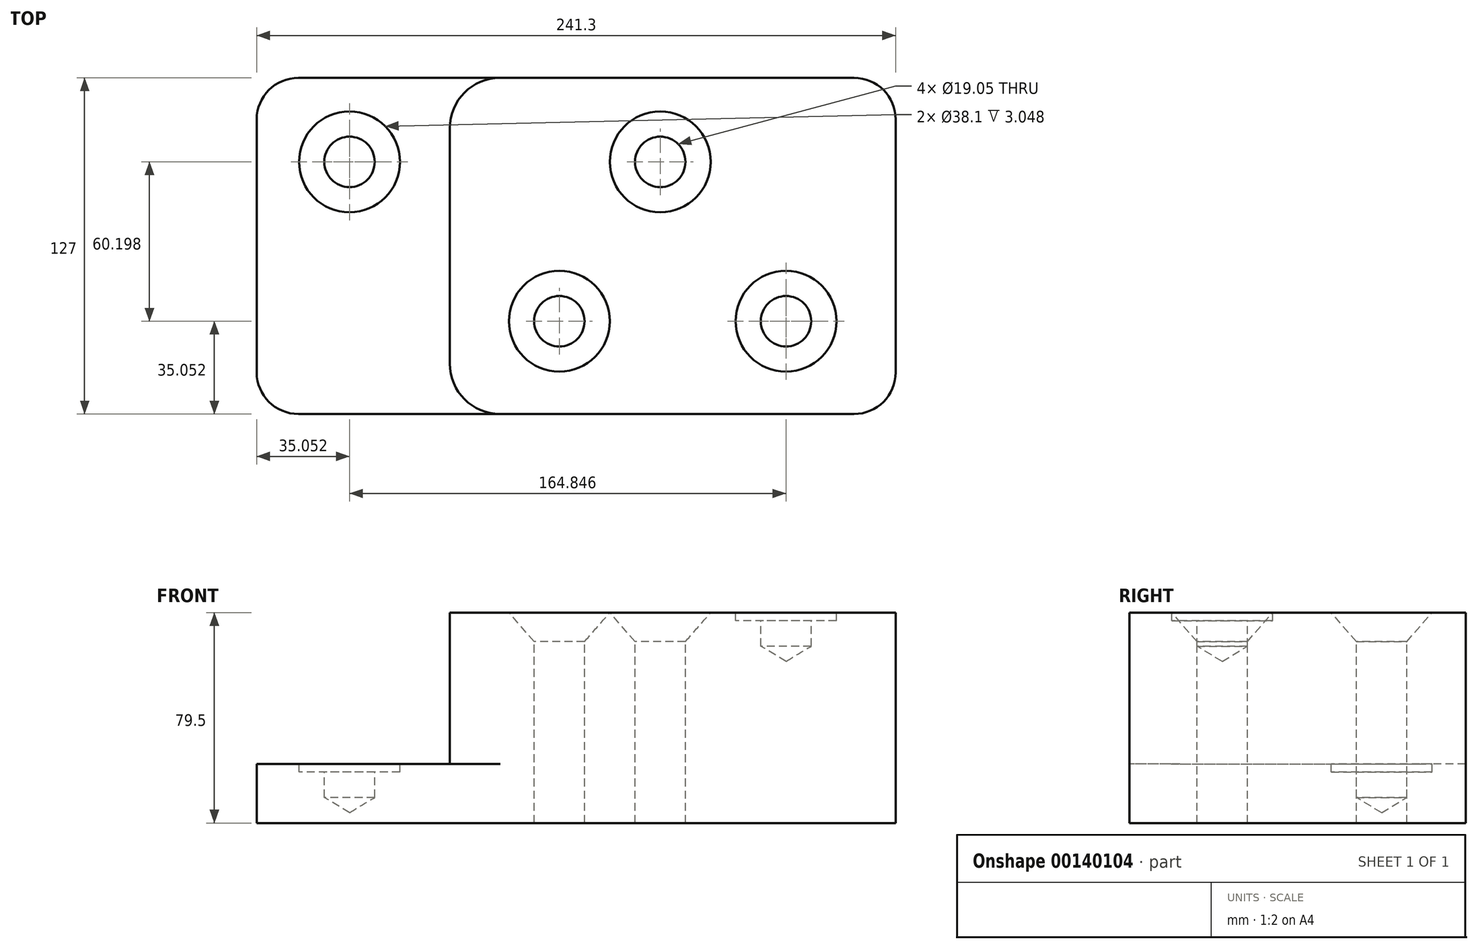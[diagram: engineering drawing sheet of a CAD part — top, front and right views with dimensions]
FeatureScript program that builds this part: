
annotation { "Feature Type Name" : "Feature", "Feature Type Description" : "" }
export const myFeature = defineFeature(function(context is Context, id is Id, definition is map)
    precondition{}
    {
        {
            var Q0;
            Q0=qCreatedBy(makeId("Top.planeOp"),FACE);
            var sketch = newSketch(context, id + "F0", { "sketchPlane" : qUnion([Q0])});
            skLineSegment(sketch, "E0.bottom", {"start": v(0, 0) * mm, "end": v(72.9, 0) * mm});
            skLineSegment(sketch, "E0.top", {"start": v(0, 127) * mm, "end": v(72.9, 127) * mm});
            skLineSegment(sketch, "E0.left", {"start": v(0, 0) * mm, "end": v(0, 127) * mm});
            skLineSegment(sketch, "E0.right", {"start": v(72.9, 0) * mm, "end": v(72.9, 127) * mm});
            skLineSegment(sketch, "E1.bottom", {"start": v(72.9, 0) * mm, "end": v(241.3, 0) * mm});
            skLineSegment(sketch, "E1.top", {"start": v(72.9, 127) * mm, "end": v(241.3, 127) * mm});
            skLineSegment(sketch, "E1.right", {"start": v(241.3, 0) * mm, "end": v(241.3, 127) * mm});
            skArc(sketch, "E2", {"start": v(91.95, 127) * mm, "mid": v(78.48, 121.42) * mm, "end": v(72.9, 107.95) * mm});
            skArc(sketch, "E3", {"start": v(72.9, 19.05) * mm, "mid": v(78.48, 5.58) * mm, "end": v(91.95, 0) * mm});
            skSolve(sketch);
        }
        {
            var Q0;
            {var subQ3=sQuery(id+"F0.wireOp",EDGE,"E2");Q0=makeQuery(id+"F0.imprint","IMPRINT",FACE,{"disambiguationData":[TD([[makeQuery(id+"F0.imprint","IMPRINT",EDGE,{"derivedFrom":subQ3}),-1.0]])]});}
            var Q1;
            {var subQ3=sQuery(id+"F0.wireOp",EDGE,"E3");Q1=makeQuery(id+"F0.imprint","IMPRINT",FACE,{"disambiguationData":[TD([[makeQuery(id+"F0.imprint","IMPRINT",EDGE,{"derivedFrom":subQ3}),-1.0]])]});}
            var Q2;
            {var subQ1=sQuery(id+"F0.wireOp",EDGE,"E0.bottom");Q2=makeQuery(id+"F0.imprint","IMPRINT",FACE,{"disambiguationData":[TD([[makeQuery(id+"F0.imprint","IMPRINT",EDGE,{"derivedFrom":subQ1}),1.0]])]});}
            extrude(context, id + "F1", {"entities" : qUnion([Q0, Q1, Q2]), "depth" : 22.35 * mm});
        }
        {
            var Q0;
            {var subQ0=sQuery(id+"F0.wireOp",EDGE,"E1.right");Q0=makeQuery(id+"F0.imprint","IMPRINT",FACE,{"disambiguationData":[TD([[makeQuery(id+"F0.imprint","IMPRINT",EDGE,{"derivedFrom":subQ0}),1.0]])]});}
            var sketch = newSketch(context, id + "F2", { "sketchPlane" : qUnion([Q0])});
            skArc(sketch, "E4.0.0", {"start": v(72.9, 19.05) * mm, "mid": v(78.48, 5.58) * mm, "end": v(91.95, 0) * mm});
            skLineSegment(sketch, "E4.0.1", {"start": v(91.95, 0) * mm, "end": v(241.3, 0) * mm});
            skLineSegment(sketch, "E4.0.2", {"start": v(241.3, 0) * mm, "end": v(241.3, 127) * mm});
            skLineSegment(sketch, "E4.0.3", {"start": v(241.3, 127) * mm, "end": v(91.95, 127) * mm});
            skArc(sketch, "E4.0.4", {"start": v(91.95, 127) * mm, "mid": v(78.48, 121.42) * mm, "end": v(72.9, 107.95) * mm});
            skLineSegment(sketch, "E4.0.5", {"start": v(72.9, 107.95) * mm, "end": v(72.9, 19.05) * mm});
            skSolve(sketch);
        }
        {
            var Q0;
            Q0 = qSketchRegion(id + "F2", true);
            extrude(context, id + "F3", {"entities" : qUnion([Q0]), "operationType" : NewBodyOperationType.ADD, "depth" : 79.5 * mm});
        }
        {
            var Q0;
            Q0=makeQuery(id+"F1.opExtrude","CAP_FACE",FACE,{"disambiguationData":[OSD([sQuery(id+"F0.wireOp",EDGE,"E0.bottom"),sQuery(id+"F0.wireOp",EDGE,"E0.top"),sQuery(id+"F0.wireOp",EDGE,"E0.left"),sQuery(id+"F0.wireOp",EDGE,"E1.bottom"),sQuery(id+"F0.wireOp",EDGE,"E1.top"),sQuery(id+"F0.wireOp",EDGE,"E0.right"),sQuery(id+"F0.wireOp",EDGE,"E2"),sQuery(id+"F0.wireOp",EDGE,"E3")])],"isStart":false});
            var sketch = newSketch(context, id + "F4", { "sketchPlane" : qUnion([Q0])});
            skCircle(sketch, "E5", {"center": v(35.05, 95.25) * mm, "radius": 9.53 * mm});
            skCircle(sketch, "E6", {"center": v(152.4, 95.25) * mm, "radius": 9.53 * mm});
            skCircle(sketch, "E7", {"center": v(114.3, 35.05) * mm, "radius": 9.53 * mm});
            skCircle(sketch, "E8", {"center": v(199.9, 35.05) * mm, "radius": 9.53 * mm});
            skSolve(sketch);
        }
        {
            var Q0;
            Q0=makeQuery(id+"F3.opExtrude","CAP_FACE",FACE,{"disambiguationData":[OSD([sQuery(id+"F2.wireOp",EDGE,"E4.0.0"),sQuery(id+"F2.wireOp",EDGE,"E4.0.1"),sQuery(id+"F2.wireOp",EDGE,"E4.0.2"),sQuery(id+"F2.wireOp",EDGE,"E4.0.3"),sQuery(id+"F2.wireOp",EDGE,"E4.0.4"),sQuery(id+"F2.wireOp",EDGE,"E4.0.5")])],"isStart":false});
            var sketch = newSketch(context, id + "F5", { "sketchPlane" : qUnion([Q0])});
            skPoint(sketch, "E9", {"position": v(152.4, 95.25) * mm});
            skPoint(sketch, "E10", {"position": v(199.9, 35.05) * mm});
            skPoint(sketch, "E11", {"position": v(114.3, 35.05) * mm});
            skPoint(sketch, "E12", {"position": v(35.05, 95.25) * mm});
            skSolve(sketch);
        }
        {
            var Q0;
            Q0=sQuery(id+"F5.wireOp",VERTEX,"E10");
            var Q1;
            Q1=sQuery(id+"F5.wireOp",VERTEX,"E12");
            var Q2;
            Q2=makeQuery(id+"F1.opExtrude","SWEPT_BODY",BODY,{"disambiguationData":[OSD([sQuery(id+"F0.wireOp",EDGE,"E0.bottom"),sQuery(id+"F0.wireOp",EDGE,"E0.top"),sQuery(id+"F0.wireOp",EDGE,"E0.left"),sQuery(id+"F0.wireOp",EDGE,"E1.bottom"),sQuery(id+"F0.wireOp",EDGE,"E1.top"),sQuery(id+"F0.wireOp",EDGE,"E0.right"),sQuery(id+"F0.wireOp",EDGE,"E2"),sQuery(id+"F0.wireOp",EDGE,"E3")])]});
            hole(context, id + "F6", {"style" : HoleStyle.C_BORE, "endStyle" : HoleEndStyle.BLIND, "holeDiameter" : 19.05 * mm, "cBoreDiameter" : 38.1 * mm, "cBoreDepth" : 3.05 * mm, "holeDepth" : 12.7 * mm, "locations" : qUnion([Q0, Q1]), "scope" : qUnion([Q2])});
        }
        {
            var Q0;
            Q0=makeQuery(id+"F3.opExtrude","CAP_FACE",FACE,{"disambiguationData":[OSD([sQuery(id+"F2.wireOp",EDGE,"E4.0.0"),sQuery(id+"F2.wireOp",EDGE,"E4.0.1"),sQuery(id+"F2.wireOp",EDGE,"E4.0.2"),sQuery(id+"F2.wireOp",EDGE,"E4.0.3"),sQuery(id+"F2.wireOp",EDGE,"E4.0.4"),sQuery(id+"F2.wireOp",EDGE,"E4.0.5")])],"isStart":false});
            var sketch = newSketch(context, id + "F7", { "sketchPlane" : qUnion([Q0])});
            skPoint(sketch, "E13", {"position": v(152.4, 95.25) * mm});
            skPoint(sketch, "E14", {"position": v(114.3, 35.05) * mm});
            skSolve(sketch);
        }
        {
            var Q0;
            Q0=sQuery(id+"F7.wireOp",VERTEX,"E13");
            var Q1;
            Q1=sQuery(id+"F7.wireOp",VERTEX,"E14");
            var Q2;
            Q2=makeQuery(id+"F1.opExtrude","SWEPT_BODY",BODY,{"disambiguationData":[OSD([sQuery(id+"F0.wireOp",EDGE,"E0.bottom"),sQuery(id+"F0.wireOp",EDGE,"E0.top"),sQuery(id+"F0.wireOp",EDGE,"E0.left"),sQuery(id+"F0.wireOp",EDGE,"E1.bottom"),sQuery(id+"F0.wireOp",EDGE,"E1.top"),sQuery(id+"F0.wireOp",EDGE,"E0.right"),sQuery(id+"F0.wireOp",EDGE,"E2"),sQuery(id+"F0.wireOp",EDGE,"E3")])]});
            hole(context, id + "F8", {"style" : HoleStyle.C_SINK, "endStyle" : HoleEndStyle.THROUGH, "holeDiameter" : 19.05 * mm, "cSinkDiameter" : 38.1 * mm, "cSinkAngle" : 82 * degree, "locations" : qUnion([Q0, Q1]), "scope" : qUnion([Q2]), "isTappedThrough" : true});
        }
        {
            var Q0;
            Q0=makeQuery(id+"F1.opExtrude","SWEPT_EDGE",EDGE,{"disambiguationData":[OSD([sQuery(id+"F0.wireOp",EDGE,"E0.bottom"),sQuery(id+"F0.wireOp",EDGE,"E0.left")])]});
            var Q1;
            Q1=makeQuery(id+"F1.opExtrude","SWEPT_EDGE",EDGE,{"disambiguationData":[OSD([sQuery(id+"F0.wireOp",EDGE,"E0.top"),sQuery(id+"F0.wireOp",EDGE,"E0.left")])]});
            var Q2;
            Q2=makeQuery(id+"F3.opExtrude","SWEPT_EDGE",EDGE,{"disambiguationData":[OSD([sQuery(id+"F2.wireOp",EDGE,"E4.0.1"),sQuery(id+"F2.wireOp",EDGE,"E4.0.2")])]});
            var Q3;
            Q3=makeQuery(id+"F3.opExtrude","SWEPT_EDGE",EDGE,{"disambiguationData":[OSD([sQuery(id+"F2.wireOp",EDGE,"E4.0.2"),sQuery(id+"F2.wireOp",EDGE,"E4.0.3")])]});
            fillet(context, id + "F9", {"entities" : qUnion([Q0, Q1, Q2, Q3]), "radius" : 15.75 * mm, "tangentPropagation" : true, "allowEdgeOverflow" : false});
        }
    });
